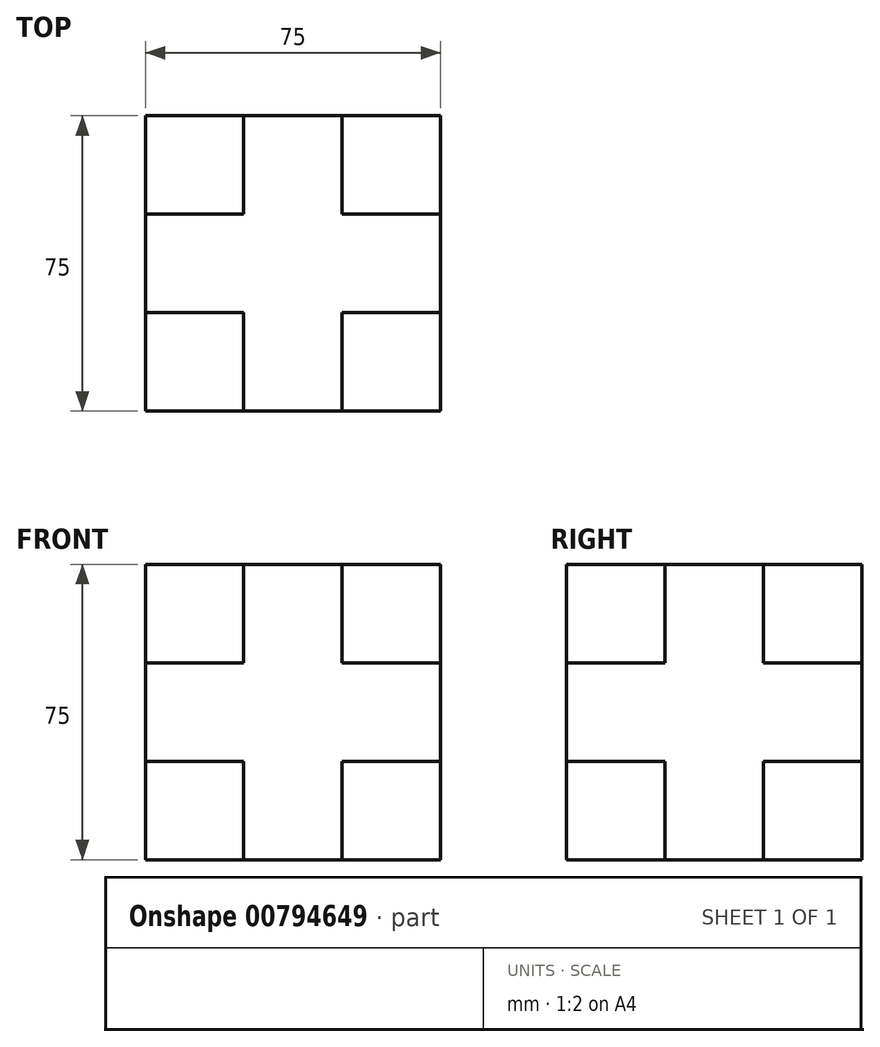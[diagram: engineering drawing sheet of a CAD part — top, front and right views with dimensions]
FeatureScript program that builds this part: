
annotation { "Feature Type Name" : "Feature", "Feature Type Description" : "" }
export const myFeature = defineFeature(function(context is Context, id is Id, definition is map)
    precondition{}
    {
        {
            var Q0;
            Q0=qCreatedBy(makeId("Top.planeOp"),FACE);
            var sketch = newSketch(context, id + "F0", { "sketchPlane" : qUnion([Q0])});
            skLineSegment(sketch, "E0.bottom", {"start": v(-49.3, 33.28) * mm, "end": v(25.7, 33.28) * mm});
            skLineSegment(sketch, "E0.top", {"start": v(-49.3, -41.72) * mm, "end": v(25.7, -41.72) * mm});
            skLineSegment(sketch, "E0.left", {"start": v(-49.3, 33.28) * mm, "end": v(-49.3, -41.72) * mm});
            skLineSegment(sketch, "E0.right", {"start": v(25.7, 33.28) * mm, "end": v(25.7, -41.72) * mm});
            skSolve(sketch);
        }
        {
            var Q0;
            Q0 = qSketchRegion(id + "F0", true);
            extrude(context, id + "F1", {"entities" : qUnion([Q0]), "depth" : 75 * mm, "offsetDistance" : 25 * mm});
        }
        {
            var Q0;
            Q0=makeQuery(id+"F1.opExtrude","CAP_FACE",FACE,{"disambiguationData":[OSD([sQuery(id+"F0.wireOp",EDGE,"E0.bottom"),sQuery(id+"F0.wireOp",EDGE,"E0.top"),sQuery(id+"F0.wireOp",EDGE,"E0.left"),sQuery(id+"F0.wireOp",EDGE,"E0.right")])],"isStart":true});
            var sketch = newSketch(context, id + "F2", { "sketchPlane" : qUnion([Q0])});
            skLineSegment(sketch, "E1.bottom", {"start": v(-49.3, 41.72) * mm, "end": v(-24.3, 41.72) * mm});
            skLineSegment(sketch, "E1.top", {"start": v(-49.3, 16.72) * mm, "end": v(-24.3, 16.72) * mm});
            skLineSegment(sketch, "E1.left", {"start": v(-49.3, 41.72) * mm, "end": v(-49.3, 16.72) * mm});
            skLineSegment(sketch, "E1.right", {"start": v(-24.3, 41.72) * mm, "end": v(-24.3, 16.72) * mm});
            skLineSegment(sketch, "E2.bottom", {"start": v(-49.3, -33.28) * mm, "end": v(-24.3, -33.28) * mm});
            skLineSegment(sketch, "E2.top", {"start": v(-49.3, -8.28) * mm, "end": v(-24.3, -8.28) * mm});
            skLineSegment(sketch, "E2.left", {"start": v(-49.3, -33.28) * mm, "end": v(-49.3, -8.28) * mm});
            skLineSegment(sketch, "E2.right", {"start": v(-24.3, -33.28) * mm, "end": v(-24.3, -8.28) * mm});
            skLineSegment(sketch, "E3.bottom", {"start": v(25.7, 41.72) * mm, "end": v(0.7, 41.72) * mm});
            skLineSegment(sketch, "E3.top", {"start": v(25.7, 16.72) * mm, "end": v(0.7, 16.72) * mm});
            skLineSegment(sketch, "E3.left", {"start": v(25.7, 41.72) * mm, "end": v(25.7, 16.72) * mm});
            skLineSegment(sketch, "E3.right", {"start": v(0.7, 41.72) * mm, "end": v(0.7, 16.72) * mm});
            skLineSegment(sketch, "E4.bottom", {"start": v(25.7, -33.28) * mm, "end": v(0.7, -33.28) * mm});
            skLineSegment(sketch, "E4.top", {"start": v(25.7, -8.28) * mm, "end": v(0.7, -8.28) * mm});
            skLineSegment(sketch, "E4.left", {"start": v(25.7, -33.28) * mm, "end": v(25.7, -8.28) * mm});
            skLineSegment(sketch, "E4.right", {"start": v(0.7, -33.28) * mm, "end": v(0.7, -8.28) * mm});
            skSolve(sketch);
        }
        {
            var Q0;
            Q0 = qSketchRegion(id + "F2", true);
            extrude(context, id + "F3", {"entities" : qUnion([Q0]), "operationType" : NewBodyOperationType.REMOVE, "oppositeDirection" : true, "depth" : 25 * mm, "offsetDistance" : 25 * mm});
        }
        {
            var Q0;
            Q0=makeQuery(id+"F1.opExtrude","CAP_FACE",FACE,{"disambiguationData":[OSD([sQuery(id+"F0.wireOp",EDGE,"E0.bottom"),sQuery(id+"F0.wireOp",EDGE,"E0.top"),sQuery(id+"F0.wireOp",EDGE,"E0.left"),sQuery(id+"F0.wireOp",EDGE,"E0.right")])],"isStart":false});
            var sketch = newSketch(context, id + "F4", { "sketchPlane" : qUnion([Q0])});
            skLineSegment(sketch, "E5.bottom", {"start": v(-49.3, 33.28) * mm, "end": v(-24.3, 33.28) * mm});
            skLineSegment(sketch, "E5.top", {"start": v(-49.3, 8.28) * mm, "end": v(-24.3, 8.28) * mm});
            skLineSegment(sketch, "E5.left", {"start": v(-49.3, 33.28) * mm, "end": v(-49.3, 8.28) * mm});
            skLineSegment(sketch, "E5.right", {"start": v(-24.3, 33.28) * mm, "end": v(-24.3, 8.28) * mm});
            skLineSegment(sketch, "E6.bottom", {"start": v(25.7, 33.28) * mm, "end": v(0.7, 33.28) * mm});
            skLineSegment(sketch, "E6.top", {"start": v(25.7, 8.28) * mm, "end": v(0.7, 8.28) * mm});
            skLineSegment(sketch, "E6.left", {"start": v(25.7, 33.28) * mm, "end": v(25.7, 8.28) * mm});
            skLineSegment(sketch, "E6.right", {"start": v(0.7, 33.28) * mm, "end": v(0.7, 8.28) * mm});
            skLineSegment(sketch, "E7.bottom", {"start": v(-49.3, -41.72) * mm, "end": v(-24.3, -41.72) * mm});
            skLineSegment(sketch, "E7.top", {"start": v(-49.3, -16.72) * mm, "end": v(-24.3, -16.72) * mm});
            skLineSegment(sketch, "E7.left", {"start": v(-49.3, -41.72) * mm, "end": v(-49.3, -16.72) * mm});
            skLineSegment(sketch, "E7.right", {"start": v(-24.3, -41.72) * mm, "end": v(-24.3, -16.72) * mm});
            skLineSegment(sketch, "E8.bottom", {"start": v(25.7, -41.72) * mm, "end": v(0.7, -41.72) * mm});
            skLineSegment(sketch, "E8.top", {"start": v(25.7, -16.72) * mm, "end": v(0.7, -16.72) * mm});
            skLineSegment(sketch, "E8.left", {"start": v(25.7, -41.72) * mm, "end": v(25.7, -16.72) * mm});
            skLineSegment(sketch, "E8.right", {"start": v(0.7, -41.72) * mm, "end": v(0.7, -16.72) * mm});
            skSolve(sketch);
        }
        {
            var Q0;
            Q0 = qSketchRegion(id + "F4", true);
            extrude(context, id + "F5", {"entities" : qUnion([Q0]), "operationType" : NewBodyOperationType.REMOVE, "oppositeDirection" : true, "depth" : 25 * mm, "offsetDistance" : 25 * mm});
        }
    });
